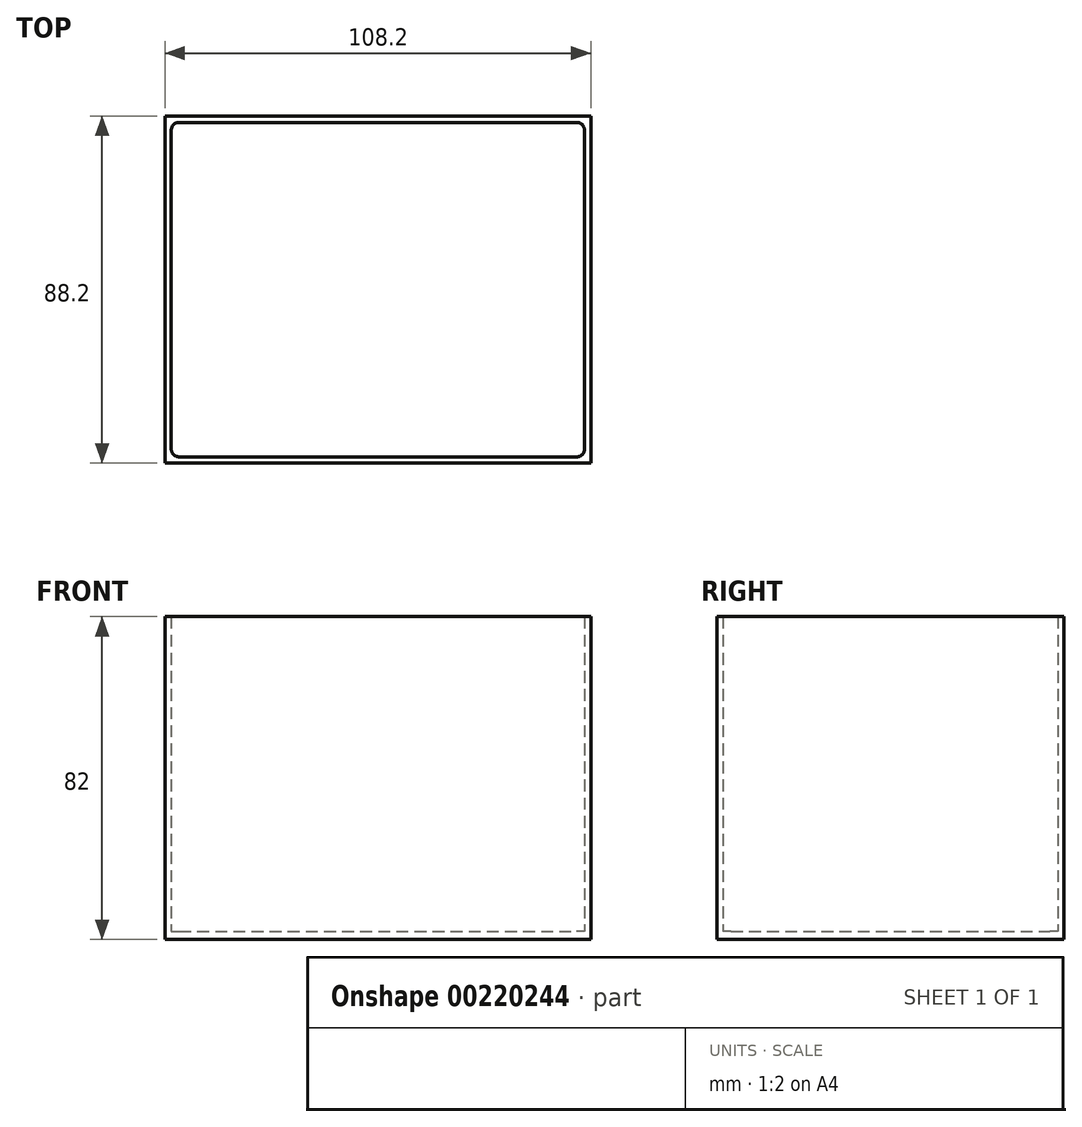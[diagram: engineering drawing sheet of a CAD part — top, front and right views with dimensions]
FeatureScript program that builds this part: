
annotation { "Feature Type Name" : "Feature", "Feature Type Description" : "" }
export const myFeature = defineFeature(function(context is Context, id is Id, definition is map)
    precondition{}
    {
        {
            var Q0;
            Q0=qCreatedBy(makeId("Top.planeOp"),FACE);
            var sketch = newSketch(context, id + "F0", { "sketchPlane" : qUnion([Q0])});
            skLineSegment(sketch, "E0.bottom", {"start": v(0, 0) * mm, "end": v(105, 0) * mm});
            skLineSegment(sketch, "E0.top", {"start": v(0, 85) * mm, "end": v(105, 85) * mm});
            skLineSegment(sketch, "E0.left", {"start": v(0, 0) * mm, "end": v(0, 85) * mm});
            skLineSegment(sketch, "E0.right", {"start": v(105, 0) * mm, "end": v(105, 85) * mm});
            skLineSegment(sketch, "E1.bottom", {"start": v(-1.6, -1.6) * mm, "end": v(106.6, -1.6) * mm});
            skLineSegment(sketch, "E1.top", {"start": v(-1.6, 86.6) * mm, "end": v(106.6, 86.6) * mm});
            skLineSegment(sketch, "E1.left", {"start": v(-1.6, -1.6) * mm, "end": v(-1.6, 86.6) * mm});
            skLineSegment(sketch, "E1.right", {"start": v(106.6, -1.6) * mm, "end": v(106.6, 86.6) * mm});
            skSolve(sketch);
        }
        {
            var Q0;
            Q0=makeQuery(id+"F0.imprint","IMPRINT",FACE,{"disambiguationData":[TD([[makeQuery(id+"F0.imprint","IMPRINT",EDGE,{"derivedFrom":sQuery(id+"F0.wireOp",EDGE,"E0.bottom")}),-1.0]])]});
            extrude(context, id + "F1", {"entities" : qUnion([Q0]), "depth" : 80 * mm});
        }
        {
            var Q0;
            Q0=makeQuery(id+"F1.opExtrude","CAP_FACE",FACE,{"disambiguationData":[OSD([sQuery(id+"F0.wireOp",EDGE,"E0.bottom"),sQuery(id+"F0.wireOp",EDGE,"E0.top"),sQuery(id+"F0.wireOp",EDGE,"E0.left"),sQuery(id+"F0.wireOp",EDGE,"E0.right"),sQuery(id+"F0.wireOp",EDGE,"E1.bottom"),sQuery(id+"F0.wireOp",EDGE,"E1.top"),sQuery(id+"F0.wireOp",EDGE,"E1.left"),sQuery(id+"F0.wireOp",EDGE,"E1.right")])],"isStart":true});
            var sketch = newSketch(context, id + "F2", { "sketchPlane" : qUnion([Q0])});
            skLineSegment(sketch, "E2.0", {"start": v(0, -85) * mm, "end": v(105, -85) * mm});
            skLineSegment(sketch, "E3.0", {"start": v(-1.6, -86.6) * mm, "end": v(106.6, -86.6) * mm});
            skLineSegment(sketch, "E4.0", {"start": v(-1.6, 1.6) * mm, "end": v(-1.6, -86.6) * mm});
            skLineSegment(sketch, "E5.0", {"start": v(-1.6, 1.6) * mm, "end": v(106.6, 1.6) * mm});
            skLineSegment(sketch, "E6.0", {"start": v(106.6, 1.6) * mm, "end": v(106.6, -86.6) * mm});
            skSolve(sketch);
        }
        {
            var Q0;
            Q0=makeQuery(id+"F2.imprint","IMPRINT",FACE,{"disambiguationData":[TD([[makeQuery(id+"F2.imprint","IMPRINT",EDGE,{"derivedFrom":sQuery(id+"F2.wireOp",EDGE,"E2.0")}),1.0]])]});
            var Q1;
            Q1=makeQuery(id+"F2.imprint","IMPRINT",FACE,{"disambiguationData":[TD([[makeQuery(id+"F2.imprint","IMPRINT",EDGE,{"derivedFrom":sQuery(id+"F2.wireOp",EDGE,"E2.0")}),-1.0]])]});
            extrude(context, id + "F3", {"entities" : qUnion([Q0, Q1]), "operationType" : NewBodyOperationType.ADD, "depth" : 2 * mm});
        }
        {
            var Q0;
            Q0=makeQuery(id+"F1.opExtrude","SWEPT_EDGE",EDGE,{"disambiguationData":[OSD([sQuery(id+"F0.wireOp",EDGE,"E0.top"),sQuery(id+"F0.wireOp",EDGE,"E0.left")])]});
            var Q1;
            Q1=makeQuery(id+"F1.opExtrude","SWEPT_EDGE",EDGE,{"disambiguationData":[OSD([sQuery(id+"F0.wireOp",EDGE,"E0.top"),sQuery(id+"F0.wireOp",EDGE,"E0.right")])]});
            var Q2;
            Q2=makeQuery(id+"F1.opExtrude","CAP_EDGE",EDGE,{"disambiguationData":[OSD([sQuery(id+"F0.wireOp",EDGE,"E0.bottom")])],"isStart":true});
            var Q3;
            Q3=makeQuery(id+"F1.opExtrude","SWEPT_EDGE",EDGE,{"disambiguationData":[OSD([sQuery(id+"F0.wireOp",EDGE,"E0.bottom"),sQuery(id+"F0.wireOp",EDGE,"E0.left")])]});
            var Q4;
            Q4=makeQuery(id+"F1.opExtrude","CAP_EDGE",EDGE,{"disambiguationData":[OSD([sQuery(id+"F0.wireOp",EDGE,"E0.left")])],"isStart":true});
            var Q5;
            Q5=makeQuery(id+"F1.opExtrude","CAP_EDGE",EDGE,{"disambiguationData":[OSD([sQuery(id+"F0.wireOp",EDGE,"E0.top")])],"isStart":true});
            var Q6;
            Q6=makeQuery(id+"F1.opExtrude","CAP_EDGE",EDGE,{"disambiguationData":[OSD([sQuery(id+"F0.wireOp",EDGE,"E0.right")])],"isStart":true});
            var Q7;
            Q7=makeQuery(id+"F1.opExtrude","SWEPT_EDGE",EDGE,{"disambiguationData":[OSD([sQuery(id+"F0.wireOp",EDGE,"E0.bottom"),sQuery(id+"F0.wireOp",EDGE,"E0.right")])]});
            fillet(context, id + "F4", {"entities" : qUnion([Q0, Q1, Q2, Q3, Q4, Q5, Q6, Q7]), "radius" : 2 * mm, "tangentPropagation" : true, "allowEdgeOverflow" : false});
        }
    });
